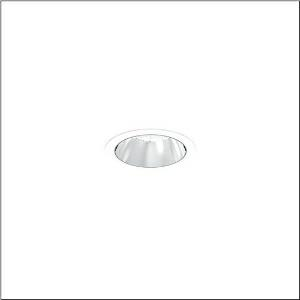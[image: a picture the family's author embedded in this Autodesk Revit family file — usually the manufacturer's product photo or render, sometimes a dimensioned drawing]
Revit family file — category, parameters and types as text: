
# Revit family: lunis_21_m_51db15mc91c
name_source: partatom
category: Lighting Fixtures
units: mm (PartAtom-declared; Revit-internal decimal feet)

## family parameters
Cut with Voids When Loaded = No
Host = Face
Light Source = No
Part Type = Normal
Room Calculation Point = No
Round Connector Dimension = Use Diameter
Shared = No

## types (1)
- --- (1 x LED, 4040 lm, 25.5 W, 6500K)
    Apparent Load = 26 VA
    CIE Flux Codes = 95 99 100 100 100
    Color Rendering = 80
    Color Temperature = 6500K
    Default Elevation = 1800 mm
    Description = Lunis 21,  M, downlight, light control with lens, of PMMA, anti glare with reflector, of PC, highly specular, light emission: direct distribution, LED rated luminous flux: 1.860lm, light colour: 830/840/865, with terminal, 3-pole, mains connection: 220..240V, AC/DC, 0/50..60Hz, housing, round, of diecast aluminium, traffic white (RAL 9016), diameter: 115mm, clamping range: 1..40mm, protection rating (complete): IP20, protection rating (on room side): IP54, insulation class (complete): insulation class II (safety insulation), certification: CE, impact resistance: IK03, packaging unit: 1 piece
    Height = 0 mm  [stored 0 ft]
    Lamp = 1 x LED
    Lamp Light Flux = 4040 lm
    Lamp Power = 25.5 W
    Lamp count = 1
    Length = 115 mm
    Luminous efficacy = 158 lm/W
    Manufacturer = Siteco
    ModVariant = No
    Model = 51DB15MC91C
    Mounting Place = Ceiling
    Mounting Type = Recessed
    Number of Poles = 1
    OnlyDefault = Yes
    Power Factor = 1
    Product Name = Lunis 21 M
    Product group = downlight
    ProductGroupID = 400
    Protection Class = Protection class II
    Protection Degree = IP 20
    RLX_Detail_Level = 1
    RLX_Emergency_Light_Flux = 0 lm
    RLX_Emergency_Type = 0
    RLX_Emergency_Type_DB = No
    RlxData = <blob elided: 14849 chars, md5=869ac7eb>
    Socket = socket
    Standby Power = 0 W
    System Light Flux = 4040 lm
    System Power = 26 W
    Type Comments = individual setting: colour temperature 6500K, luminous flux: 100 % | (ON | ON | OFF | OFF) | 700 mA
    Type Image = l_1290850.jpg
    URL = http://relux.com
    VarID = @adj_020648
    Voltage = 0 V
    Weight = 0.00 kg
    Width = 0 mm  [stored 0 ft]

note: [stored X ft] marks values corroborated as IEEE doubles in the binary element streams (Revit-internal decimal feet)

## geometry (parser evidence)
native form markers: Sweep x11
no freeform markers — native parametric forms only
